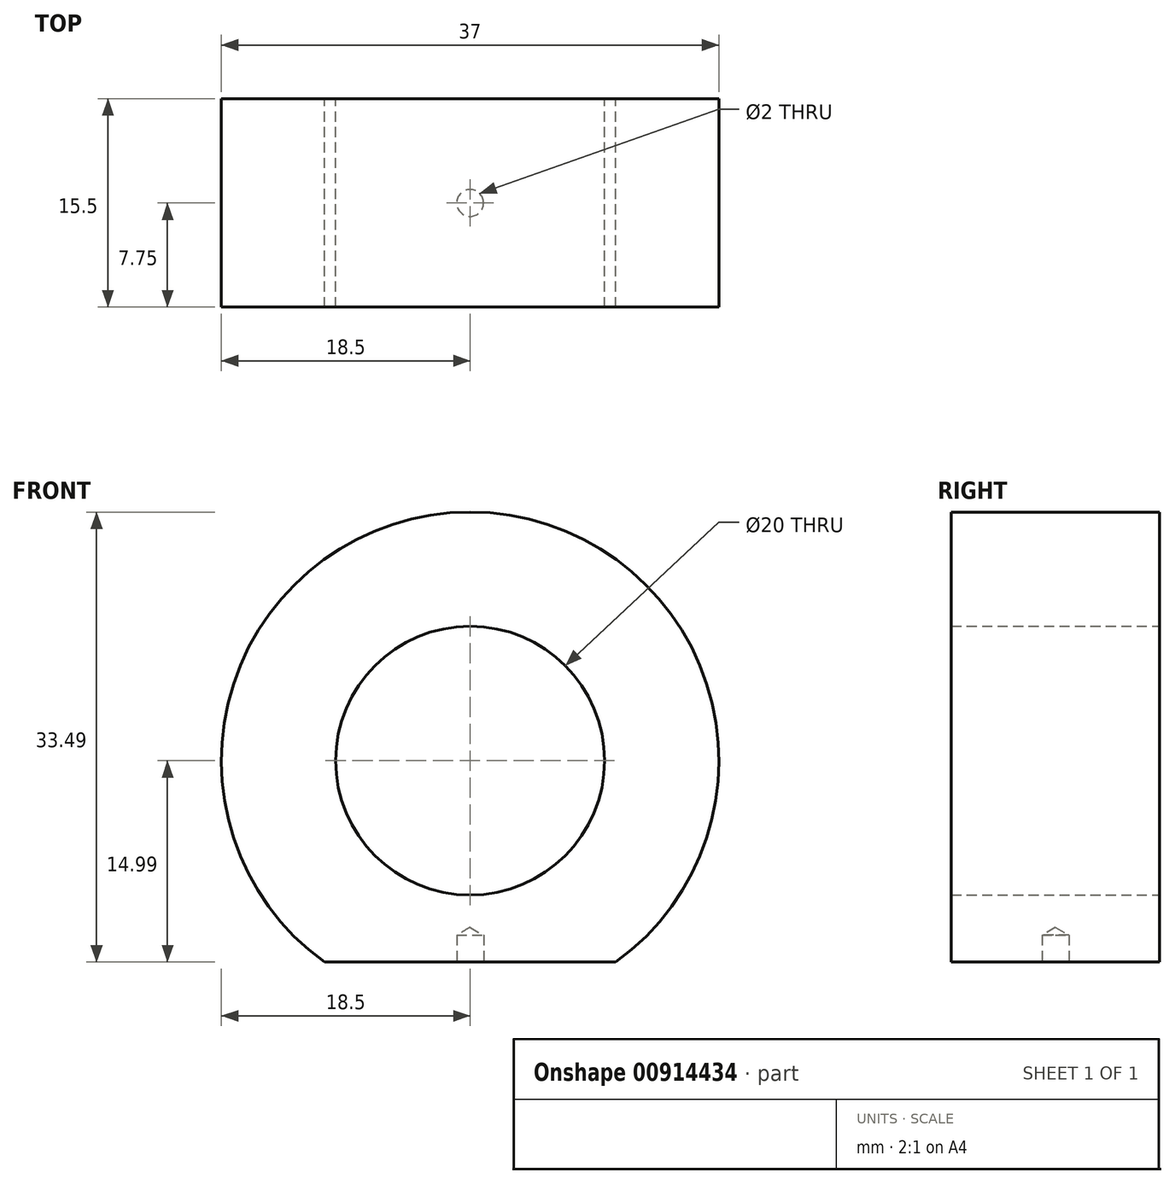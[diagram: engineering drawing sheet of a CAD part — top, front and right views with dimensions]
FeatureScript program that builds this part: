
annotation { "Feature Type Name" : "Feature", "Feature Type Description" : "" }
export const myFeature = defineFeature(function(context is Context, id is Id, definition is map)
    precondition{}
    {
        {
            var Q0;
            Q0=qCreatedBy(makeId("Front.planeOp"),FACE);
            var sketch = newSketch(context, id + "F0", { "sketchPlane" : qUnion([Q0])});
            skCircle(sketch, "E0", {"center": v(0, 0) * mm, "radius": 10 * mm});
            skArc(sketch, "E1", {"start": v(10.84, -15) * mm, "mid": v(0, 18.5) * mm, "end": v(-10.84, -15) * mm});
            skLineSegment(sketch, "E2", {"start": v(-10.84, -15) * mm, "end": v(10.84, -15) * mm});
            skSolve(sketch);
        }
        {
            var Q0;
            Q0 = qSketchRegion(id + "F0", true);
            extrude(context, id + "F1", {"entities" : qUnion([Q0]), "depth" : 15.5 * mm, "offsetDistance" : 25 * mm});
        }
        {
            var Q0;
            Q0=makeQuery(id+"F1.opExtrude","SWEPT_FACE",FACE,{"disambiguationData":[OSD([sQuery(id+"F0.wireOp",EDGE,"E2")])]});
            var sketch = newSketch(context, id + "F2", { "sketchPlane" : qUnion([Q0])});
            skCircle(sketch, "E3", {"center": v(0, 7.75) * mm, "radius": 2.33 * mm});
            skSolve(sketch);
        }
        {
            var Q0;
            Q0=sQuery(id+"F2.wireOp",VERTEX,"E3.center");
            var Q1;
            Q1=makeQuery(id+"F1.opExtrude","SWEPT_BODY",BODY,{"disambiguationData":[OSD([sQuery(id+"F0.wireOp",EDGE,"E0"),sQuery(id+"F0.wireOp",EDGE,"E1"),sQuery(id+"F0.wireOp",EDGE,"E2")])]});
            hole(context, id + "F3", {"style" : HoleStyle.SIMPLE, "endStyle" : HoleEndStyle.BLIND, "holeDiameter" : 2 * mm, "majorDiameter" : 5 * mm, "holeDepth" : 2 * mm, "isTappedThrough" : true, "tappedDepth" : 13.5 * mm, "tapClearance" : 3, "locations" : qUnion([Q0]), "scope" : qUnion([Q1])});
        }
    });
